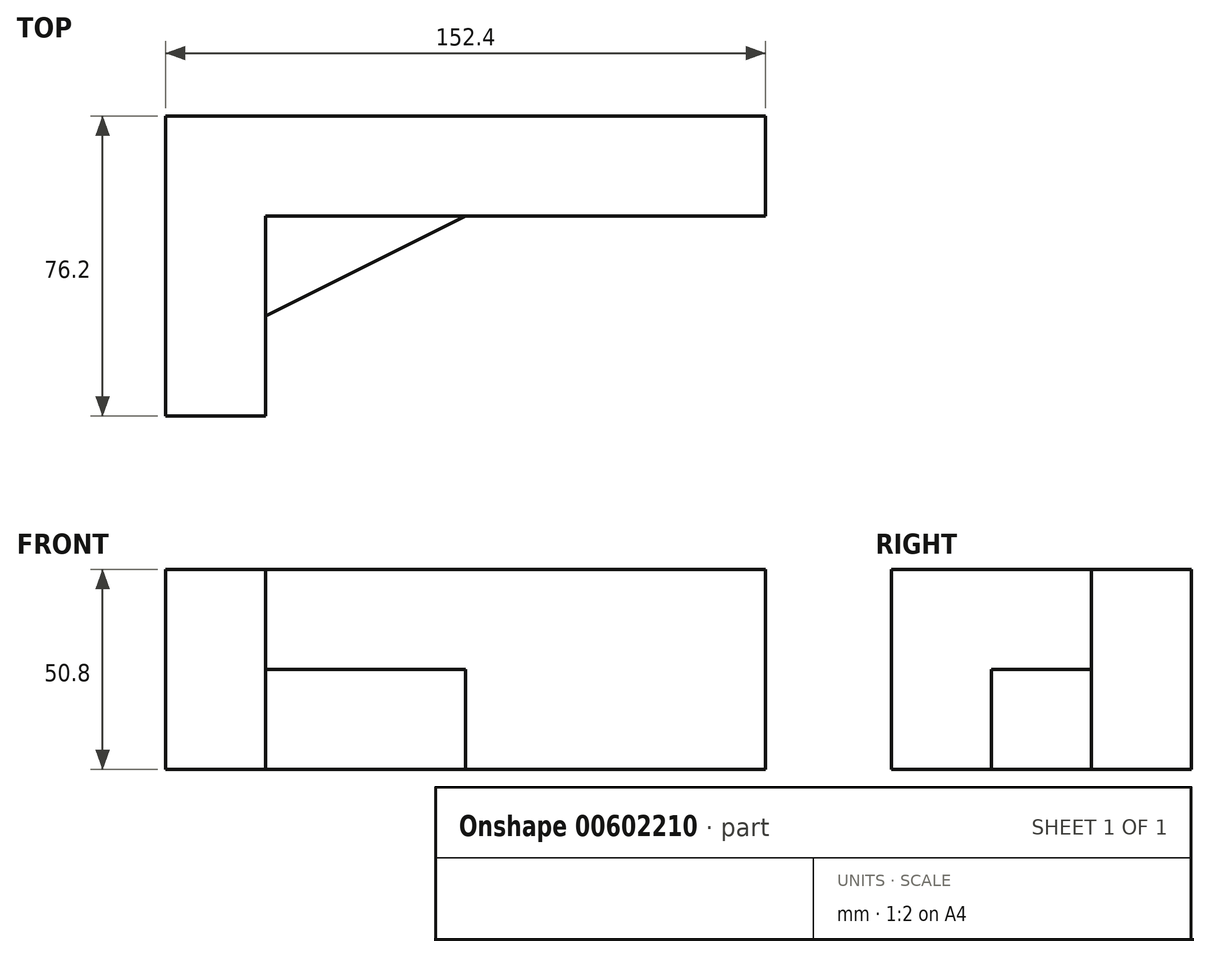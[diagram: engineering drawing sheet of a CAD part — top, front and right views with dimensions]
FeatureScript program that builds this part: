
annotation { "Feature Type Name" : "Feature", "Feature Type Description" : "" }
export const myFeature = defineFeature(function(context is Context, id is Id, definition is map)
    precondition{}
    {
        {
            var Q0;
            Q0=qCreatedBy(makeId("Top.planeOp"),FACE);
            var sketch = newSketch(context, id + "F0", { "sketchPlane" : qUnion([Q0])});
            skLineSegment(sketch, "E0", {"start": v(0, 0) * mm, "end": v(0, 76.2) * mm});
            skLineSegment(sketch, "E1", {"start": v(0, 76.2) * mm, "end": v(152.4, 76.2) * mm});
            skLineSegment(sketch, "E2", {"start": v(152.4, 76.2) * mm, "end": v(152.4, 50.8) * mm});
            skLineSegment(sketch, "E3", {"start": v(152.4, 50.8) * mm, "end": v(25.4, 50.8) * mm});
            skLineSegment(sketch, "E4", {"start": v(25.4, 50.8) * mm, "end": v(25.4, 0) * mm});
            skLineSegment(sketch, "E5", {"start": v(25.4, 0) * mm, "end": v(0, 0) * mm});
            skSolve(sketch);
        }
        {
            var Q0;
            Q0=makeQuery(id+"F0.imprint","IMPRINT",FACE,{"disambiguationData":[TD([[makeQuery(id+"F0.imprint","IMPRINT",EDGE,{"derivedFrom":sQuery(id+"F0.wireOp",EDGE,"E0")}),-1.0]])]});
            extrude(context, id + "F1", {"entities" : qUnion([Q0]), "oppositeDirection" : true, "depth" : 50.8 * mm, "offsetDistance" : 25.4 * mm});
        }
        {
            var Q0;
            Q0=makeQuery(id+"F1.opExtrude","SWEPT_FACE",FACE,{"disambiguationData":[OSD([sQuery(id+"F0.wireOp",EDGE,"E3")])]});
            var sketch = newSketch(context, id + "F2", { "sketchPlane" : qUnion([Q0])});
            skLineSegment(sketch, "E6", {"start": v(25.4, -50.8) * mm, "end": v(25.4, -25.4) * mm});
            skLineSegment(sketch, "E7", {"start": v(25.4, -25.4) * mm, "end": v(76.2, -25.4) * mm});
            skLineSegment(sketch, "E8", {"start": v(76.2, -25.4) * mm, "end": v(76.2, -50.8) * mm});
            skLineSegment(sketch, "E9", {"start": v(76.2, -50.8) * mm, "end": v(25.4, -50.8) * mm});
            skSolve(sketch);
        }
        {
            var Q0;
            Q0=makeQuery(id+"F2.imprint","IMPRINT",FACE,{"disambiguationData":[TD([[makeQuery(id+"F2.imprint","IMPRINT",EDGE,{"derivedFrom":sQuery(id+"F2.wireOp",EDGE,"E6")}),-1.0]])]});
            extrude(context, id + "F3", {"entities" : qUnion([Q0]), "operationType" : NewBodyOperationType.ADD, "depth" : 25.4 * mm, "offsetDistance" : 25.4 * mm});
        }
        {
            var Q0;
            Q0=makeQuery(id+"F3.opExtrude","SWEPT_FACE",FACE,{"disambiguationData":[OSD([sQuery(id+"F2.wireOp",EDGE,"E7")])]});
            var sketch = newSketch(context, id + "F4", { "sketchPlane" : qUnion([Q0])});
            skLineSegment(sketch, "E10", {"start": v(25.4, 25.4) * mm, "end": v(76.2, 50.8) * mm});
            skSolve(sketch);
        }
        {
            var Q0;
            Q0=makeQuery(id+"F4.imprint","IMPRINT",FACE,{"disambiguationData":[TD([[makeQuery(id+"F4.imprint","IMPRINT",EDGE,{"derivedFrom":sQuery(id+"F4.wireOp",EDGE,"E10")}),-1.0]])]});
            extrude(context, id + "F5", {"entities" : qUnion([Q0]), "operationType" : NewBodyOperationType.REMOVE, "oppositeDirection" : true, "depth" : 25.4 * mm, "offsetDistance" : 25.4 * mm});
        }
    });
